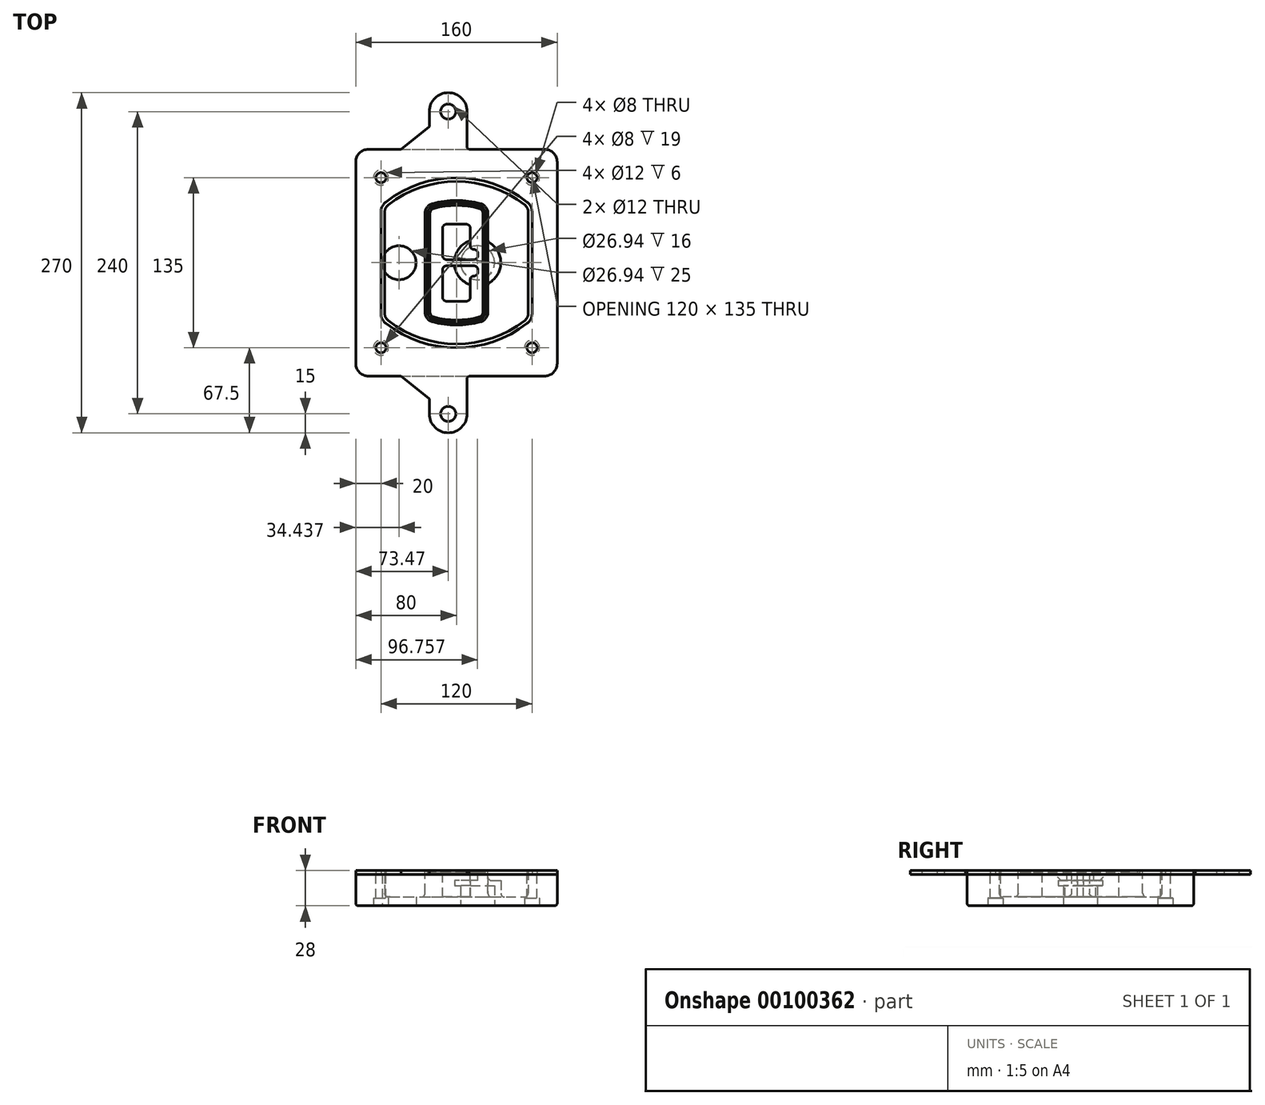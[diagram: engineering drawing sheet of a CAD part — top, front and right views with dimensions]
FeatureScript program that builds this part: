
annotation { "Feature Type Name" : "Feature", "Feature Type Description" : "" }
export const myFeature = defineFeature(function(context is Context, id is Id, definition is map)
    precondition{}
    {
        {
            var Q0;
            Q0=qCreatedBy(makeId("Top.planeOp"),FACE);
            var sketch = newSketch(context, id + "F0", { "sketchPlane" : qUnion([Q0])});
            skPoint(sketch, "E0.rect.middle", {"position": v(0, 0) * mm});
            skLineSegment(sketch, "E1.bottom", {"start": v(-70, -90) * mm, "end": v(70, -90) * mm});
            skLineSegment(sketch, "E1.top", {"start": v(-70, 90) * mm, "end": v(70, 90) * mm});
            skLineSegment(sketch, "E1.left", {"start": v(-80, -80) * mm, "end": v(-80, 80) * mm});
            skLineSegment(sketch, "E1.right", {"start": v(80, -80) * mm, "end": v(80, 80) * mm});
            skLineSegment(sketch, "E2", {"start": v(-80, 90) * mm, "end": v(80, -90) * mm, "construction": true});
            skLineSegment(sketch, "E3", {"start": v(80, 90) * mm, "end": v(-80, -90) * mm, "construction": true});
            skCircle(sketch, "E4", {"center": v(-60, 67.5) * mm, "radius": 4 * mm});
            skCircle(sketch, "E5", {"center": v(60, 67.5) * mm, "radius": 4 * mm});
            skCircle(sketch, "E6", {"center": v(60, -67.5) * mm, "radius": 4 * mm});
            skCircle(sketch, "E7", {"center": v(-60, -67.5) * mm, "radius": 4 * mm});
            skLineSegment(sketch, "E8", {"start": v(-60, 67.5) * mm, "end": v(60, 67.5) * mm, "construction": true});
            skLineSegment(sketch, "E9", {"start": v(60, 67.5) * mm, "end": v(60, -67.5) * mm, "construction": true});
            skLineSegment(sketch, "E10", {"start": v(60, -67.5) * mm, "end": v(-60, -67.5) * mm, "construction": true});
            skLineSegment(sketch, "E11", {"start": v(-60, -67.5) * mm, "end": v(-60, 67.5) * mm, "construction": true});
            skLineSegment(sketch, "E12", {"start": v(-60, 40.3) * mm, "end": v(-60, -40.3) * mm});
            skLineSegment(sketch, "E13", {"start": v(60, 40.3) * mm, "end": v(60, -40.3) * mm});
            skArc(sketch, "E14", {"start": v(56.15, 48.18) * mm, "mid": v(0, 67.5) * mm, "end": v(-56.15, 48.18) * mm});
            skArc(sketch, "E15", {"start": v(-56.15, -48.18) * mm, "mid": v(0, -67.5) * mm, "end": v(56.15, -48.18) * mm});
            skLineSegment(sketch, "E16", {"start": v(-60, 0) * mm, "end": v(60, 0) * mm, "construction": true});
            skPoint(sketch, "E17.visualSharp", {"position": v(-60, -45) * mm});
            skArc(sketch, "E17.filletArc", {"start": v(-60, -40.3) * mm, "mid": v(-58.99, -44.68) * mm, "end": v(-56.15, -48.18) * mm});
            skPoint(sketch, "E18.visualSharp", {"position": v(-60, 45) * mm});
            skArc(sketch, "E18.filletArc", {"start": v(-56.15, 48.18) * mm, "mid": v(-58.99, 44.68) * mm, "end": v(-60, 40.3) * mm});
            skPoint(sketch, "E19.visualSharp", {"position": v(60, 45) * mm});
            skArc(sketch, "E19.filletArc", {"start": v(60, 40.3) * mm, "mid": v(58.99, 44.68) * mm, "end": v(56.15, 48.18) * mm});
            skPoint(sketch, "E20.visualSharp", {"position": v(60, -45) * mm});
            skArc(sketch, "E20.filletArc", {"start": v(56.15, -48.18) * mm, "mid": v(58.99, -44.68) * mm, "end": v(60, -40.3) * mm});
            skPoint(sketch, "E21.visualSharp", {"position": v(-80, 90) * mm});
            skArc(sketch, "E21.filletArc", {"start": v(-70, 90) * mm, "mid": v(-77.07, 87.07) * mm, "end": v(-80, 80) * mm});
            skPoint(sketch, "E22.visualSharp", {"position": v(80, 90) * mm});
            skArc(sketch, "E22.filletArc", {"start": v(80, 80) * mm, "mid": v(77.07, 87.07) * mm, "end": v(70, 90) * mm});
            skPoint(sketch, "E23.visualSharp", {"position": v(80, -90) * mm});
            skArc(sketch, "E23.filletArc", {"start": v(70, -90) * mm, "mid": v(77.07, -87.07) * mm, "end": v(80, -80) * mm});
            skPoint(sketch, "E24.visualSharp", {"position": v(-80, -90) * mm});
            skArc(sketch, "E24.filletArc", {"start": v(-80, -80) * mm, "mid": v(-77.07, -87.07) * mm, "end": v(-70, -90) * mm});
            skArc(sketch, "E25.0", {"start": v(57, 40.3) * mm, "mid": v(56.3, 43.36) * mm, "end": v(54.3, 45.81) * mm});
            skLineSegment(sketch, "E25.1", {"start": v(57, 40.3) * mm, "end": v(57, -40.3) * mm});
            skArc(sketch, "E25.2", {"start": v(54.3, -45.81) * mm, "mid": v(56.3, -43.36) * mm, "end": v(57, -40.3) * mm});
            skArc(sketch, "E25.3", {"start": v(-54.3, -45.81) * mm, "mid": v(0, -64.5) * mm, "end": v(54.3, -45.81) * mm});
            skArc(sketch, "E25.4", {"start": v(-57, -40.3) * mm, "mid": v(-56.3, -43.36) * mm, "end": v(-54.3, -45.81) * mm});
            skArc(sketch, "E25.5", {"start": v(54.3, 45.81) * mm, "mid": v(0, 64.5) * mm, "end": v(-54.3, 45.81) * mm});
            skLineSegment(sketch, "E25.6", {"start": v(-57, 40.3) * mm, "end": v(-57, -40.3) * mm});
            skArc(sketch, "E25.7", {"start": v(-54.3, 45.81) * mm, "mid": v(-56.3, 43.36) * mm, "end": v(-57, 40.3) * mm});
            skArc(sketch, "E26.0", {"start": v(-58.62, 51.33) * mm, "mid": v(-62.58, 46.43) * mm, "end": v(-64, 40.3) * mm});
            skArc(sketch, "E26.1", {"start": v(58.62, 51.33) * mm, "mid": v(0, 71.5) * mm, "end": v(-58.62, 51.33) * mm});
            skArc(sketch, "E26.2", {"start": v(64, 40.3) * mm, "mid": v(62.58, 46.43) * mm, "end": v(58.62, 51.33) * mm});
            skLineSegment(sketch, "E26.3", {"start": v(64, 40.3) * mm, "end": v(64, -40.3) * mm});
            skArc(sketch, "E26.4", {"start": v(58.62, -51.33) * mm, "mid": v(62.58, -46.43) * mm, "end": v(64, -40.3) * mm});
            skLineSegment(sketch, "E26.5", {"start": v(-64, 40.3) * mm, "end": v(-64, -40.3) * mm});
            skArc(sketch, "E26.6", {"start": v(-58.62, -51.33) * mm, "mid": v(0, -71.5) * mm, "end": v(58.62, -51.33) * mm});
            skArc(sketch, "E26.7", {"start": v(-64, -40.3) * mm, "mid": v(-62.58, -46.43) * mm, "end": v(-58.62, -51.33) * mm});
            skSolve(sketch);
        }
        {
            var Q0;
            Q0=makeQuery(id+"F0.imprint","IMPRINT",FACE,{"disambiguationData":[TD([[makeQuery(id+"F0.imprint","IMPRINT",EDGE,{"derivedFrom":sQuery(id+"F0.wireOp",EDGE,"E1.bottom")}),1.0]])]});
            var Q1;
            Q1=makeQuery(id+"F0.imprint","IMPRINT",FACE,{"disambiguationData":[TD([[makeQuery(id+"F0.imprint","IMPRINT",EDGE,{"derivedFrom":sQuery(id+"F0.wireOp",EDGE,"E12")}),1.0]])]});
            var Q2;
            Q2=makeQuery(id+"F0.imprint","IMPRINT",FACE,{"disambiguationData":[TD([[makeQuery(id+"F0.imprint","IMPRINT",EDGE,{"derivedFrom":sQuery(id+"F0.wireOp",EDGE,"E25.0")}),1.0]])]});
            var Q3;
            Q3=makeQuery(id+"F0.imprint","IMPRINT",FACE,{"disambiguationData":[TD([[makeQuery(id+"F0.imprint","IMPRINT",EDGE,{"derivedFrom":sQuery(id+"F0.wireOp",EDGE,"E12")}),-1.0]])]});
            extrude(context, id + "F1", {"entities" : qUnion([Q0, Q1, Q2, Q3]), "oppositeDirection" : true, "depth" : 25 * mm});
        }
        {
            var Q0;
            Q0=makeQuery(id+"F0.imprint","IMPRINT",FACE,{"disambiguationData":[TD([[makeQuery(id+"F0.imprint","IMPRINT",EDGE,{"derivedFrom":sQuery(id+"F0.wireOp",EDGE,"E12")}),1.0]])]});
            extrude(context, id + "F2", {"entities" : qUnion([Q0]), "operationType" : NewBodyOperationType.ADD, "depth" : 3 * mm});
        }
        {
            var Q0;
            Q0=makeQuery(id+"F0.imprint","IMPRINT",FACE,{"disambiguationData":[TD([[makeQuery(id+"F0.imprint","IMPRINT",EDGE,{"derivedFrom":sQuery(id+"F0.wireOp",EDGE,"E25.0")}),1.0]])]});
            extrude(context, id + "F3", {"entities" : qUnion([Q0]), "operationType" : NewBodyOperationType.REMOVE, "oppositeDirection" : true, "depth" : 18 * mm});
        }
        {
            var Q0;
            Q0=makeQuery(id+"F2.opExtrude","CAP_FACE",FACE,{"disambiguationData":[OSD([sQuery(id+"F0.wireOp",EDGE,"E12"),sQuery(id+"F0.wireOp",EDGE,"E13"),sQuery(id+"F0.wireOp",EDGE,"E14"),sQuery(id+"F0.wireOp",EDGE,"E15"),sQuery(id+"F0.wireOp",EDGE,"E17.filletArc"),sQuery(id+"F0.wireOp",EDGE,"E18.filletArc"),sQuery(id+"F0.wireOp",EDGE,"E19.filletArc"),sQuery(id+"F0.wireOp",EDGE,"E20.filletArc"),sQuery(id+"F0.wireOp",EDGE,"E25.0"),sQuery(id+"F0.wireOp",EDGE,"E25.1"),sQuery(id+"F0.wireOp",EDGE,"E25.2"),sQuery(id+"F0.wireOp",EDGE,"E25.3"),sQuery(id+"F0.wireOp",EDGE,"E25.4"),sQuery(id+"F0.wireOp",EDGE,"E25.5"),sQuery(id+"F0.wireOp",EDGE,"E25.6"),sQuery(id+"F0.wireOp",EDGE,"E25.7")])],"isStart":false});
            var sketch = newSketch(context, id + "F4", { "sketchPlane" : qUnion([Q0])});
            skArc(sketch, "E27.0", {"start": v(-19.08, -46.97) * mm, "mid": v(0, -49.5) * mm, "end": v(19.08, -46.97) * mm});
            skArc(sketch, "E28.0", {"start": v(19.08, 46.97) * mm, "mid": v(0, 49.5) * mm, "end": v(-19.08, 46.97) * mm});
            skLineSegment(sketch, "E29", {"start": v(-25, 39.25) * mm, "end": v(-25, -39.25) * mm});
            skLineSegment(sketch, "E30", {"start": v(25, 39.25) * mm, "end": v(25, -39.25) * mm});
            skLineSegment(sketch, "E31", {"start": v(-25, 45.1) * mm, "end": v(25, 45.1) * mm, "construction": true});
            skLineSegment(sketch, "E32", {"start": v(-25, -45.1) * mm, "end": v(25, -45.1) * mm, "construction": true});
            skPoint(sketch, "E33.visualSharp", {"position": v(-25, 45.1) * mm});
            skArc(sketch, "E33.filletArc", {"start": v(-19.08, 46.97) * mm, "mid": v(-23.35, 44.11) * mm, "end": v(-25, 39.25) * mm});
            skPoint(sketch, "E34.visualSharp", {"position": v(25, 45.1) * mm});
            skArc(sketch, "E34.filletArc", {"start": v(25, 39.25) * mm, "mid": v(23.35, 44.11) * mm, "end": v(19.08, 46.97) * mm});
            skPoint(sketch, "E35.visualSharp", {"position": v(25, -45.1) * mm});
            skArc(sketch, "E35.filletArc", {"start": v(19.08, -46.97) * mm, "mid": v(23.35, -44.11) * mm, "end": v(25, -39.25) * mm});
            skPoint(sketch, "E36.visualSharp", {"position": v(-25, -45.1) * mm});
            skArc(sketch, "E36.filletArc", {"start": v(-25, -39.25) * mm, "mid": v(-23.35, -44.11) * mm, "end": v(-19.08, -46.97) * mm});
            skArc(sketch, "E37.0", {"start": v(54.3, 45.81) * mm, "mid": v(0, 64.5) * mm, "end": v(-54.3, 45.81) * mm});
            skArc(sketch, "E37.1", {"start": v(-54.3, 45.81) * mm, "mid": v(-56.3, 43.36) * mm, "end": v(-57, 40.3) * mm});
            skLineSegment(sketch, "E37.2", {"start": v(-57, 40.3) * mm, "end": v(-57, -40.3) * mm});
            skArc(sketch, "E37.3", {"start": v(-57, -40.3) * mm, "mid": v(-56.3, -43.36) * mm, "end": v(-54.3, -45.81) * mm});
            skArc(sketch, "E37.4", {"start": v(-54.3, -45.81) * mm, "mid": v(0, -64.5) * mm, "end": v(54.3, -45.81) * mm});
            skArc(sketch, "E37.5", {"start": v(54.3, -45.81) * mm, "mid": v(56.3, -43.36) * mm, "end": v(57, -40.3) * mm});
            skLineSegment(sketch, "E37.6", {"start": v(57, 40.3) * mm, "end": v(57, -40.3) * mm});
            skArc(sketch, "E37.7", {"start": v(57, 40.3) * mm, "mid": v(56.3, 43.36) * mm, "end": v(54.3, 45.81) * mm});
            skLineSegment(sketch, "E38.0", {"start": v(23, 39.25) * mm, "end": v(23, -39.25) * mm});
            skArc(sketch, "E38.1", {"start": v(18.56, -45.04) * mm, "mid": v(21.76, -42.9) * mm, "end": v(23, -39.25) * mm});
            skArc(sketch, "E38.2", {"start": v(-18.56, -45.04) * mm, "mid": v(0, -47.5) * mm, "end": v(18.56, -45.04) * mm});
            skArc(sketch, "E38.3", {"start": v(-23, -39.25) * mm, "mid": v(-21.76, -42.9) * mm, "end": v(-18.56, -45.04) * mm});
            skLineSegment(sketch, "E38.4", {"start": v(-23, 39.25) * mm, "end": v(-23, -39.25) * mm});
            skArc(sketch, "E38.5", {"start": v(23, 39.25) * mm, "mid": v(21.76, 42.9) * mm, "end": v(18.56, 45.04) * mm});
            skArc(sketch, "E38.6", {"start": v(-18.56, 45.04) * mm, "mid": v(-21.76, 42.9) * mm, "end": v(-23, 39.25) * mm});
            skArc(sketch, "E38.7", {"start": v(18.56, 45.04) * mm, "mid": v(0, 47.5) * mm, "end": v(-18.56, 45.04) * mm});
            skArc(sketch, "E39.0", {"start": v(21, 39.25) * mm, "mid": v(20.18, 41.68) * mm, "end": v(18.04, 43.1) * mm});
            skLineSegment(sketch, "E39.1", {"start": v(21, 39.25) * mm, "end": v(21, -39.25) * mm});
            skArc(sketch, "E39.2", {"start": v(18.04, -43.1) * mm, "mid": v(20.18, -41.68) * mm, "end": v(21, -39.25) * mm});
            skArc(sketch, "E39.3", {"start": v(-18.04, -43.1) * mm, "mid": v(0, -45.5) * mm, "end": v(18.04, -43.1) * mm});
            skArc(sketch, "E39.4", {"start": v(-21, -39.25) * mm, "mid": v(-20.18, -41.68) * mm, "end": v(-18.04, -43.1) * mm});
            skArc(sketch, "E39.5", {"start": v(18.04, 43.1) * mm, "mid": v(0, 45.5) * mm, "end": v(-18.04, 43.1) * mm});
            skLineSegment(sketch, "E39.6", {"start": v(-21, 39.25) * mm, "end": v(-21, -39.25) * mm});
            skArc(sketch, "E39.7", {"start": v(-18.04, 43.1) * mm, "mid": v(-20.18, 41.68) * mm, "end": v(-21, 39.25) * mm});
            skLineSegment(sketch, "E40", {"start": v(-25, 0) * mm, "end": v(25, 0) * mm, "construction": true});
            skLineSegment(sketch, "E41", {"start": v(-11, 5.5) * mm, "end": v(-11, 27.5) * mm});
            skLineSegment(sketch, "E42", {"start": v(-8, 30.5) * mm, "end": v(8, 30.5) * mm});
            skLineSegment(sketch, "E43", {"start": v(11, 27.5) * mm, "end": v(11, 13.5) * mm});
            skLineSegment(sketch, "E44", {"start": v(14, 10.5) * mm, "end": v(14, 10.5) * mm});
            skLineSegment(sketch, "E45", {"start": v(17, 7.5) * mm, "end": v(17, 5.5) * mm});
            skLineSegment(sketch, "E46", {"start": v(14, 2.5) * mm, "end": v(-8, 2.5) * mm});
            skPoint(sketch, "E47.visualSharp", {"position": v(-11, 30.5) * mm});
            skArc(sketch, "E47.filletArc", {"start": v(-8, 30.5) * mm, "mid": v(-10.12, 29.62) * mm, "end": v(-11, 27.5) * mm});
            skPoint(sketch, "E48.visualSharp", {"position": v(11, 30.5) * mm});
            skArc(sketch, "E48.filletArc", {"start": v(11, 27.5) * mm, "mid": v(10.12, 29.62) * mm, "end": v(8, 30.5) * mm});
            skPoint(sketch, "E49.visualSharp", {"position": v(11, 10.5) * mm});
            skArc(sketch, "E49.filletArc", {"start": v(11, 13.5) * mm, "mid": v(11.88, 11.38) * mm, "end": v(14, 10.5) * mm});
            skPoint(sketch, "E50.visualSharp", {"position": v(17, 10.5) * mm});
            skArc(sketch, "E50.filletArc", {"start": v(17, 7.5) * mm, "mid": v(16.12, 9.62) * mm, "end": v(14, 10.5) * mm});
            skPoint(sketch, "E51.visualSharp", {"position": v(17, 2.5) * mm});
            skArc(sketch, "E51.filletArc", {"start": v(14, 2.5) * mm, "mid": v(16.12, 3.38) * mm, "end": v(17, 5.5) * mm});
            skPoint(sketch, "E52.visualSharp", {"position": v(-11, 2.5) * mm});
            skArc(sketch, "E52.filletArc", {"start": v(-11, 5.5) * mm, "mid": v(-10.12, 3.38) * mm, "end": v(-8, 2.5) * mm});
            skLineSegment(sketch, "E53.0.MirrorCS", {"start": v(14, -2.5) * mm, "end": v(-8, -2.5) * mm});
            skArc(sketch, "E54.0.MirrorCS", {"start": v(-11, -5.5) * mm, "mid": v(-10.12, -3.38) * mm, "end": v(-8, -2.5) * mm});
            skLineSegment(sketch, "E55.0.MirrorCS", {"start": v(-11, -5.5) * mm, "end": v(-11, -27.5) * mm});
            skArc(sketch, "E56.0.MirrorCS", {"start": v(-8, -30.5) * mm, "mid": v(-10.12, -29.62) * mm, "end": v(-11, -27.5) * mm});
            skLineSegment(sketch, "E57.0.MirrorCS", {"start": v(-8, -30.5) * mm, "end": v(8, -30.5) * mm});
            skArc(sketch, "E58.0.MirrorCS", {"start": v(11, -27.5) * mm, "mid": v(10.12, -29.62) * mm, "end": v(8, -30.5) * mm});
            skLineSegment(sketch, "E59.0.MirrorCS", {"start": v(11, -27.5) * mm, "end": v(11, -13.5) * mm});
            skArc(sketch, "E60.0.MirrorCS", {"start": v(11, -13.5) * mm, "mid": v(11.88, -11.38) * mm, "end": v(14, -10.5) * mm});
            skArc(sketch, "E61.0.MirrorCS", {"start": v(17, -7.5) * mm, "mid": v(16.12, -9.62) * mm, "end": v(14, -10.5) * mm});
            skLineSegment(sketch, "E62.0.MirrorCS", {"start": v(17, -7.5) * mm, "end": v(17, -5.5) * mm});
            skArc(sketch, "E63.0.MirrorCS", {"start": v(14, -2.5) * mm, "mid": v(16.12, -3.38) * mm, "end": v(17, -5.5) * mm});
            skSolve(sketch);
        }
        {
            var Q0;
            Q0=makeQuery(id+"F4.imprint","IMPRINT",FACE,{"disambiguationData":[TD([[makeQuery(id+"F4.imprint","IMPRINT",EDGE,{"derivedFrom":sQuery(id+"F4.wireOp",EDGE,"E27.0")}),1.0]])]});
            var Q1;
            Q1=makeQuery(id+"F4.imprint","IMPRINT",FACE,{"disambiguationData":[TD([[makeQuery(id+"F4.imprint","IMPRINT",EDGE,{"derivedFrom":sQuery(id+"F4.wireOp",EDGE,"E38.0")}),-1.0]])]});
            var Q2;
            Q2=makeQuery(id+"F4.imprint","IMPRINT",FACE,{"disambiguationData":[TD([[makeQuery(id+"F4.imprint","IMPRINT",EDGE,{"derivedFrom":sQuery(id+"F4.wireOp",EDGE,"E39.0")}),1.0]])]});
            extrude(context, id + "F5", {"entities" : qUnion([Q0, Q1, Q2]), "operationType" : NewBodyOperationType.ADD, "endBound" : BoundingType.UP_TO_NEXT, "oppositeDirection" : true, "depth" : 25 * mm});
        }
        {
            var Q0;
            Q0=makeQuery(id+"F4.imprint","IMPRINT",FACE,{"disambiguationData":[TD([[makeQuery(id+"F4.imprint","IMPRINT",EDGE,{"derivedFrom":sQuery(id+"F4.wireOp",EDGE,"E38.0")}),-1.0]])]});
            extrude(context, id + "F6", {"entities" : qUnion([Q0]), "operationType" : NewBodyOperationType.REMOVE, "oppositeDirection" : true, "depth" : 2 * mm});
        }
        {
            var Q0;
            Q0=makeQuery(id+"F1.opExtrude","CAP_FACE",FACE,{"disambiguationData":[OSD([sQuery(id+"F0.wireOp",EDGE,"E1.bottom"),sQuery(id+"F0.wireOp",EDGE,"E1.top"),sQuery(id+"F0.wireOp",EDGE,"E1.left"),sQuery(id+"F0.wireOp",EDGE,"E1.right"),sQuery(id+"F0.wireOp",EDGE,"E4"),sQuery(id+"F0.wireOp",EDGE,"E5"),sQuery(id+"F0.wireOp",EDGE,"E6"),sQuery(id+"F0.wireOp",EDGE,"E7"),sQuery(id+"F0.wireOp",EDGE,"E21.filletArc"),sQuery(id+"F0.wireOp",EDGE,"E22.filletArc"),sQuery(id+"F0.wireOp",EDGE,"E23.filletArc"),sQuery(id+"F0.wireOp",EDGE,"E24.filletArc")])],"isStart":false});
            var sketch = newSketch(context, id + "F7", { "sketchPlane" : qUnion([Q0])});
            skCircle(sketch, "E64", {"center": v(16.76, 0) * mm, "radius": 13.47 * mm});
            skCircle(sketch, "E65", {"center": v(-45.56, 0) * mm, "radius": 13.47 * mm});
            skLineSegment(sketch, "E66", {"start": v(80, 0) * mm, "end": v(-80, 0) * mm});
            skCircle(sketch, "E67", {"center": v(16.76, 0) * mm, "radius": 18.47 * mm});
            skCircle(sketch, "E68", {"center": v(60, -67.5) * mm, "radius": 6 * mm});
            skCircle(sketch, "E69", {"center": v(-60, -67.5) * mm, "radius": 6 * mm});
            skCircle(sketch, "E70", {"center": v(-60, 67.5) * mm, "radius": 6 * mm});
            skCircle(sketch, "E71", {"center": v(60, 67.5) * mm, "radius": 6 * mm});
            skSolve(sketch);
        }
        {
            var Q0;
            {var subQ1=sQuery(id+"F7.wireOp",EDGE,"E66");var subQ4=sQuery(id+"F7.wireOp",EDGE,"E64");var subQ6=makeQuery(id+"F7.imprint","INTERSECT",VERTEX,{"disambiguationData":[OD(0.0)],"derivedFrom":[subQ4,subQ1]});Q0=makeQuery(id+"F7.imprint","IMPRINT",FACE,{"disambiguationData":[TD([[makeQuery(id+"F7.imprint","IMPRINT",EDGE,{"disambiguationData":[TD([[subQ6,-1.0]])],"derivedFrom":subQ4}),-1.0]])]});}
            var Q1;
            {var subQ0=sQuery(id+"F7.wireOp",EDGE,"E66");var subQ1=sQuery(id+"F7.wireOp",EDGE,"E64");var subQ3=makeQuery(id+"F7.imprint","INTERSECT",VERTEX,{"disambiguationData":[OD(0.0)],"derivedFrom":[subQ1,subQ0]});Q1=makeQuery(id+"F7.imprint","IMPRINT",FACE,{"disambiguationData":[TD([[makeQuery(id+"F7.imprint","IMPRINT",EDGE,{"disambiguationData":[TD([[subQ3,-1.0]])],"derivedFrom":subQ1}),1.0]])]});}
            var Q2;
            {var subQ0=sQuery(id+"F7.wireOp",EDGE,"E66");var subQ1=sQuery(id+"F7.wireOp",EDGE,"E64");var subQ3=makeQuery(id+"F7.imprint","INTERSECT",VERTEX,{"disambiguationData":[OD(0.0)],"derivedFrom":[subQ1,subQ0]});Q2=makeQuery(id+"F7.imprint","IMPRINT",FACE,{"disambiguationData":[TD([[makeQuery(id+"F7.imprint","IMPRINT",EDGE,{"disambiguationData":[TD([[subQ3,1.0]])],"derivedFrom":subQ1}),1.0]])]});}
            var Q3;
            {var subQ1=sQuery(id+"F7.wireOp",EDGE,"E66");var subQ4=sQuery(id+"F7.wireOp",EDGE,"E64");var subQ6=makeQuery(id+"F7.imprint","INTERSECT",VERTEX,{"disambiguationData":[OD(0.0)],"derivedFrom":[subQ4,subQ1]});Q3=makeQuery(id+"F7.imprint","IMPRINT",FACE,{"disambiguationData":[TD([[makeQuery(id+"F7.imprint","IMPRINT",EDGE,{"disambiguationData":[TD([[subQ6,1.0]])],"derivedFrom":subQ4}),-1.0]])]});}
            extrude(context, id + "F8", {"entities" : qUnion([Q0, Q1, Q2, Q3]), "operationType" : NewBodyOperationType.ADD, "oppositeDirection" : true, "depth" : 20 * mm});
        }
        {
            var Q0;
            {var subQ0=sQuery(id+"F7.wireOp",EDGE,"E66");var subQ1=sQuery(id+"F7.wireOp",EDGE,"E64");var subQ3=makeQuery(id+"F7.imprint","INTERSECT",VERTEX,{"disambiguationData":[OD(0.0)],"derivedFrom":[subQ1,subQ0]});Q0=makeQuery(id+"F7.imprint","IMPRINT",FACE,{"disambiguationData":[TD([[makeQuery(id+"F7.imprint","IMPRINT",EDGE,{"disambiguationData":[TD([[subQ3,-1.0]])],"derivedFrom":subQ1}),1.0]])]});}
            var Q1;
            {var subQ0=sQuery(id+"F7.wireOp",EDGE,"E66");var subQ1=sQuery(id+"F7.wireOp",EDGE,"E64");var subQ3=makeQuery(id+"F7.imprint","INTERSECT",VERTEX,{"disambiguationData":[OD(0.0)],"derivedFrom":[subQ1,subQ0]});Q1=makeQuery(id+"F7.imprint","IMPRINT",FACE,{"disambiguationData":[TD([[makeQuery(id+"F7.imprint","IMPRINT",EDGE,{"disambiguationData":[TD([[subQ3,1.0]])],"derivedFrom":subQ1}),1.0]])]});}
            extrude(context, id + "F9", {"entities" : qUnion([Q0, Q1]), "operationType" : NewBodyOperationType.REMOVE, "oppositeDirection" : true, "depth" : 16 * mm});
        }
        {
            var Q0;
            {var subQ0=sQuery(id+"F7.wireOp",EDGE,"E66");var subQ1=sQuery(id+"F7.wireOp",EDGE,"E65");var subQ3=makeQuery(id+"F7.imprint","INTERSECT",VERTEX,{"disambiguationData":[OD(0.0)],"derivedFrom":[subQ1,subQ0]});Q0=makeQuery(id+"F7.imprint","IMPRINT",FACE,{"disambiguationData":[TD([[makeQuery(id+"F7.imprint","IMPRINT",EDGE,{"disambiguationData":[TD([[subQ3,-1.0]])],"derivedFrom":subQ1}),1.0]])]});}
            var Q1;
            {var subQ0=sQuery(id+"F7.wireOp",EDGE,"E66");var subQ1=sQuery(id+"F7.wireOp",EDGE,"E65");var subQ3=makeQuery(id+"F7.imprint","INTERSECT",VERTEX,{"disambiguationData":[OD(0.0)],"derivedFrom":[subQ1,subQ0]});Q1=makeQuery(id+"F7.imprint","IMPRINT",FACE,{"disambiguationData":[TD([[makeQuery(id+"F7.imprint","IMPRINT",EDGE,{"disambiguationData":[TD([[subQ3,1.0]])],"derivedFrom":subQ1}),1.0]])]});}
            extrude(context, id + "F10", {"entities" : qUnion([Q0, Q1]), "operationType" : NewBodyOperationType.REMOVE, "oppositeDirection" : true, "depth" : 25 * mm});
        }
        {
            var Q0;
            Q0=makeQuery(id+"F7.imprint","IMPRINT",FACE,{"disambiguationData":[TD([[makeQuery(id+"F7.imprint","IMPRINT",EDGE,{"derivedFrom":sQuery(id+"F7.wireOp",EDGE,"E68")}),1.0]])]});
            var Q1;
            Q1=makeQuery(id+"F7.imprint","IMPRINT",FACE,{"disambiguationData":[TD([[makeQuery(id+"F7.imprint","IMPRINT",EDGE,{"derivedFrom":makeQuery(id+"F1.opExtrude","CAP_EDGE",EDGE,{"disambiguationData":[OSD([sQuery(id+"F0.wireOp",EDGE,"E5")])],"isStart":false})}),-1.0]])]});
            var Q2;
            Q2=makeQuery(id+"F7.imprint","IMPRINT",FACE,{"disambiguationData":[TD([[makeQuery(id+"F7.imprint","IMPRINT",EDGE,{"derivedFrom":sQuery(id+"F7.wireOp",EDGE,"E69")}),1.0]])]});
            var Q3;
            Q3=makeQuery(id+"F7.imprint","IMPRINT",FACE,{"disambiguationData":[TD([[makeQuery(id+"F7.imprint","IMPRINT",EDGE,{"derivedFrom":makeQuery(id+"F1.opExtrude","CAP_EDGE",EDGE,{"disambiguationData":[OSD([sQuery(id+"F0.wireOp",EDGE,"E4")])],"isStart":false})}),-1.0]])]});
            var Q4;
            Q4=makeQuery(id+"F7.imprint","IMPRINT",FACE,{"disambiguationData":[TD([[makeQuery(id+"F7.imprint","IMPRINT",EDGE,{"derivedFrom":sQuery(id+"F7.wireOp",EDGE,"E70")}),1.0]])]});
            var Q5;
            Q5=makeQuery(id+"F7.imprint","IMPRINT",FACE,{"disambiguationData":[TD([[makeQuery(id+"F7.imprint","IMPRINT",EDGE,{"derivedFrom":makeQuery(id+"F1.opExtrude","CAP_EDGE",EDGE,{"disambiguationData":[OSD([sQuery(id+"F0.wireOp",EDGE,"E7")])],"isStart":false})}),-1.0]])]});
            var Q6;
            Q6=makeQuery(id+"F7.imprint","IMPRINT",FACE,{"disambiguationData":[TD([[makeQuery(id+"F7.imprint","IMPRINT",EDGE,{"derivedFrom":sQuery(id+"F7.wireOp",EDGE,"E71")}),1.0]])]});
            var Q7;
            Q7=makeQuery(id+"F7.imprint","IMPRINT",FACE,{"disambiguationData":[TD([[makeQuery(id+"F7.imprint","IMPRINT",EDGE,{"derivedFrom":makeQuery(id+"F1.opExtrude","CAP_EDGE",EDGE,{"disambiguationData":[OSD([sQuery(id+"F0.wireOp",EDGE,"E6")])],"isStart":false})}),-1.0]])]});
            extrude(context, id + "F11", {"entities" : qUnion([Q0, Q1, Q2, Q3, Q4, Q5, Q6, Q7]), "operationType" : NewBodyOperationType.REMOVE, "oppositeDirection" : true, "depth" : 6 * mm});
        }
        {
            var Q0;
            Q0=makeQuery(id+"F9.boolean.opBoolean","COPY",FACE,{"derivedFrom":makeQuery(id+"F9.opExtrude","CAP_FACE",FACE,{"disambiguationData":[OSD([sQuery(id+"F7.wireOp",EDGE,"E64")])],"isStart":false})});
            var sketch = newSketch(context, id + "F12", { "sketchPlane" : qUnion([Q0])});
            skArc(sketch, "E72.0", {"start": v(11, 17.55) * mm, "mid": v(2.57, 11.82) * mm, "end": v(-1.54, 2.5) * mm});
            skArc(sketch, "E72.1", {"start": v(-1.54, -2.5) * mm, "mid": v(2.57, -11.82) * mm, "end": v(11, -17.55) * mm});
            skLineSegment(sketch, "E73", {"start": v(-1.54, -2.5) * mm, "end": v(14, -2.5) * mm});
            skLineSegment(sketch, "E74.0", {"start": v(14, 2.5) * mm, "end": v(-1.54, 2.5) * mm});
            skArc(sketch, "E74.1", {"start": v(14, 2.5) * mm, "mid": v(16.12, 3.38) * mm, "end": v(17, 5.5) * mm});
            skLineSegment(sketch, "E74.2", {"start": v(17, 7.5) * mm, "end": v(17, 5.5) * mm});
            skArc(sketch, "E74.3", {"start": v(17, 7.5) * mm, "mid": v(16.12, 9.62) * mm, "end": v(14, 10.5) * mm});
            skArc(sketch, "E74.4", {"start": v(11, 13.5) * mm, "mid": v(11.88, 11.38) * mm, "end": v(14, 10.5) * mm});
            skLineSegment(sketch, "E74.5", {"start": v(11, 17.55) * mm, "end": v(11, 13.5) * mm});
            skLineSegment(sketch, "E74.7", {"start": v(14, -2.5) * mm, "end": v(-1.54, -2.5) * mm});
            skArc(sketch, "E74.8", {"start": v(14, -2.5) * mm, "mid": v(16.12, -3.38) * mm, "end": v(17, -5.5) * mm});
            skLineSegment(sketch, "E74.9", {"start": v(17, -7.5) * mm, "end": v(17, -5.5) * mm});
            skArc(sketch, "E74.10", {"start": v(17, -7.5) * mm, "mid": v(16.12, -9.62) * mm, "end": v(14, -10.5) * mm});
            skArc(sketch, "E74.11", {"start": v(11, -13.5) * mm, "mid": v(11.88, -11.38) * mm, "end": v(14, -10.5) * mm});
            skLineSegment(sketch, "E74.12", {"start": v(11, -17.55) * mm, "end": v(11, -13.5) * mm});
            skPoint(sketch, "E75.orphan", {"position": v(11, -27.5) * mm});
            skPoint(sketch, "E76.orphan", {"position": v(-8, -2.5) * mm});
            skPoint(sketch, "E77.orphan", {"position": v(-8, 2.5) * mm});
            skPoint(sketch, "E78.orphan", {"position": v(11, 27.5) * mm});
            skSolve(sketch);
        }
        {
            var Q0;
            {var subQ7=sQuery(id+"F12.wireOp",EDGE,"E72.0");var subQ14=sQuery(id+"F12.wireOp",EDGE,"E72.1");var subQ16=sQuery(id+"F12.wireOp",EDGE,"E74.1");var subQ18=sQuery(id+"F12.wireOp",EDGE,"E74.8");Q0=qUnion([makeQuery(id+"F12.imprint","IMPRINT",FACE,{"disambiguationData":[TD([[makeQuery(id+"F12.imprint","IMPRINT",EDGE,{"derivedFrom":subQ7}),1.0]])]}),makeQuery(id+"F12.imprint","IMPRINT",FACE,{"disambiguationData":[TD([[makeQuery(id+"F12.imprint","IMPRINT",EDGE,{"derivedFrom":subQ14}),1.0]])]}),makeQuery(id+"F12.imprint","IMPRINT",FACE,{"disambiguationData":[TD([[makeQuery(id+"F12.imprint","IMPRINT",EDGE,{"derivedFrom":subQ16}),1.0]])]}),makeQuery(id+"F12.imprint","IMPRINT",FACE,{"disambiguationData":[TD([[makeQuery(id+"F12.imprint","IMPRINT",EDGE,{"derivedFrom":subQ18}),-1.0]])]})]);}
            var Q1;
            Q1=makeQuery(id+"F5.boolean.opBoolean","SPLIT",FACE,{"disambiguationData":[TD([makeQuery(id+"F5.opExtrude","SWEPT_FACE",FACE,{"disambiguationData":[OSD([sQuery(id+"F4.wireOp",EDGE,"E41")])]})])],"derivedFrom":makeQuery(id+"F3.boolean.opBoolean","COPY",FACE,{"derivedFrom":makeQuery(id+"F3.opExtrude","CAP_FACE",FACE,{"disambiguationData":[OSD([sQuery(id+"F0.wireOp",EDGE,"E25.0"),sQuery(id+"F0.wireOp",EDGE,"E25.1"),sQuery(id+"F0.wireOp",EDGE,"E25.2"),sQuery(id+"F0.wireOp",EDGE,"E25.3"),sQuery(id+"F0.wireOp",EDGE,"E25.4"),sQuery(id+"F0.wireOp",EDGE,"E25.5"),sQuery(id+"F0.wireOp",EDGE,"E25.6"),sQuery(id+"F0.wireOp",EDGE,"E25.7")])],"isStart":false})})});
            extrude(context, id + "F13", {"entities" : qUnion([Q0]), "operationType" : NewBodyOperationType.REMOVE, "endBound" : BoundingType.UP_TO_SURFACE, "endBoundEntityFace" : qUnion([Q1]), "depth" : 25 * mm});
        }
        {
            var Q0;
            Q0=makeQuery(id+"F3.boolean.opBoolean","COPY",EDGE,{"derivedFrom":makeQuery(id+"F3.opExtrude","CAP_EDGE",EDGE,{"disambiguationData":[OSD([sQuery(id+"F0.wireOp",EDGE,"E25.6")])],"isStart":false})});
            var Q1;
            Q1=makeQuery(id+"F8.boolean.opBoolean","INTERSECT",EDGE,{"derivedFrom":[makeQuery(id+"F5.opExtrude","SWEPT_FACE",FACE,{"disambiguationData":[OSD([sQuery(id+"F4.wireOp",EDGE,"E30")])]}),makeQuery(id+"F8.opExtrude","CAP_FACE",FACE,{"disambiguationData":[OSD([sQuery(id+"F7.wireOp",EDGE,"E67")])],"isStart":false})]});
            var Q2;
            Q2=makeQuery(id+"F8.boolean.opBoolean","INTERSECT",EDGE,{"disambiguationData":[OD(1.0)],"derivedFrom":[makeQuery(id+"F5.opExtrude","SWEPT_FACE",FACE,{"disambiguationData":[OSD([sQuery(id+"F4.wireOp",EDGE,"E30")])]}),makeQuery(id+"F8.opExtrude","SWEPT_FACE",FACE,{"disambiguationData":[OSD([sQuery(id+"F7.wireOp",EDGE,"E67")])]})]});
            var Q3;
            {var subQ0=sQuery(id+"F4.wireOp",EDGE,"E30");Q3=makeQuery(id+"F8.boolean.opBoolean","SPLIT",EDGE,{"disambiguationData":[TD([makeQuery(id+"F5.opExtrude","SWEPT_FACE",FACE,{"disambiguationData":[OSD([sQuery(id+"F4.wireOp",EDGE,"E35.filletArc")])]})])],"derivedFrom":makeQuery(id+"F5.opExtrude","CAP_EDGE",EDGE,{"disambiguationData":[OSD([subQ0])],"isStart":false})});}
            var Q4;
            {var subQ0=sQuery(id+"F0.wireOp",EDGE,"E25.7");var subQ1=sQuery(id+"F0.wireOp",EDGE,"E25.1");var subQ2=sQuery(id+"F0.wireOp",EDGE,"E25.6");var subQ3=sQuery(id+"F0.wireOp",EDGE,"E25.5");var subQ4=sQuery(id+"F0.wireOp",EDGE,"E25.4");var subQ5=sQuery(id+"F0.wireOp",EDGE,"E25.0");var subQ6=sQuery(id+"F0.wireOp",EDGE,"E25.2");var subQ7=sQuery(id+"F0.wireOp",EDGE,"E25.3");Q4=makeQuery(id+"F8.boolean.opBoolean","INTERSECT",EDGE,{"derivedFrom":[makeQuery(id+"F5.boolean.opBoolean","SPLIT",FACE,{"disambiguationData":[TD([makeQuery(id+"F2.opExtrude","SWEPT_FACE",FACE,{"disambiguationData":[OSD([subQ5])]})])],"derivedFrom":makeQuery(id+"F3.boolean.opBoolean","COPY",FACE,{"derivedFrom":makeQuery(id+"F3.opExtrude","CAP_FACE",FACE,{"disambiguationData":[OSD([subQ5,subQ1,subQ6,subQ7,subQ4,subQ3,subQ2,subQ0])],"isStart":false})})}),makeQuery(id+"F8.opExtrude","SWEPT_FACE",FACE,{"disambiguationData":[OSD([sQuery(id+"F7.wireOp",EDGE,"E67")])]})]});}
            var Q5;
            Q5=makeQuery(id+"F8.boolean.opBoolean","INTERSECT",EDGE,{"disambiguationData":[OD(0.0)],"derivedFrom":[makeQuery(id+"F5.opExtrude","SWEPT_FACE",FACE,{"disambiguationData":[OSD([sQuery(id+"F4.wireOp",EDGE,"E30")])]}),makeQuery(id+"F8.opExtrude","SWEPT_FACE",FACE,{"disambiguationData":[OSD([sQuery(id+"F7.wireOp",EDGE,"E67")])]})]});
            fillet(context, id + "F14", {"entities" : qUnion([Q0, Q1, Q2, Q3, Q4, Q5]), "radius" : 3 * mm, "tangentPropagation" : true, "allowEdgeOverflow" : false});
        }
        {
            var Q0;
            Q0=makeQuery(id+"F1.opExtrude","CAP_EDGE",EDGE,{"disambiguationData":[OSD([sQuery(id+"F0.wireOp",EDGE,"E1.bottom")])],"isStart":false});
            fillet(context, id + "F15", {"entities" : qUnion([Q0]), "radius" : 2 * mm, "tangentPropagation" : true, "allowEdgeOverflow" : false});
        }
        {
            var Q0;
            {var subQ0=sQuery(id+"F0.wireOp",EDGE,"E22.filletArc");var subQ1=sQuery(id+"F0.wireOp",EDGE,"E7");var subQ2=sQuery(id+"F0.wireOp",EDGE,"E6");var subQ3=sQuery(id+"F0.wireOp",EDGE,"E5");var subQ4=sQuery(id+"F0.wireOp",EDGE,"E4");var subQ5=sQuery(id+"F0.wireOp",EDGE,"E1.bottom");var subQ6=sQuery(id+"F0.wireOp",EDGE,"E21.filletArc");var subQ7=sQuery(id+"F0.wireOp",EDGE,"E1.top");var subQ8=sQuery(id+"F0.wireOp",EDGE,"E1.left");var subQ9=sQuery(id+"F0.wireOp",EDGE,"E1.right");var subQ10=sQuery(id+"F0.wireOp",EDGE,"E23.filletArc");var subQ11=sQuery(id+"F0.wireOp",EDGE,"E24.filletArc");Q0=makeQuery(id+"F2.boolean.opBoolean","SPLIT",FACE,{"disambiguationData":[TD([makeQuery(id+"F1.opExtrude","SWEPT_FACE",FACE,{"disambiguationData":[OSD([subQ5])]})])],"derivedFrom":makeQuery(id+"F1.opExtrude","CAP_FACE",FACE,{"disambiguationData":[OSD([subQ5,subQ7,subQ8,subQ9,subQ4,subQ3,subQ2,subQ1,subQ6,subQ0,subQ10,subQ11])],"isStart":true})});}
            var sketch = newSketch(context, id + "F16", { "sketchPlane" : qUnion([Q0])});
            skLineSegment(sketch, "E79", {"start": v(-21.53, 108) * mm, "end": v(-21.53, 120) * mm});
            skLineSegment(sketch, "E80", {"start": v(9.83, 90) * mm, "end": v(8.47, 91.36) * mm});
            skLineSegment(sketch, "E81", {"start": v(8.47, 91.36) * mm, "end": v(8.47, 120) * mm});
            skLineSegment(sketch, "E82", {"start": v(-6.53, 120) * mm, "end": v(-6.53, 90) * mm, "construction": true});
            skCircle(sketch, "E83", {"center": v(-6.53, 120) * mm, "radius": 6 * mm});
            skArc(sketch, "E84", {"start": v(8.47, 120) * mm, "mid": v(-6.53, 135) * mm, "end": v(-21.53, 120) * mm});
            skLineSegment(sketch, "E85.trimOffspring", {"start": v(-21.53, 108) * mm, "end": v(-44.03, 90) * mm});
            skLineSegment(sketch, "E86", {"start": v(-80, 0) * mm, "end": v(80, 0) * mm, "construction": true});
            skLineSegment(sketch, "E87.MirrorCS", {"start": v(-21.53, -108) * mm, "end": v(-21.53, -120) * mm});
            skLineSegment(sketch, "E88.MirrorCS", {"start": v(-6.53, -120) * mm, "end": v(-6.53, -90) * mm, "construction": true});
            skCircle(sketch, "E89.MirrorC", {"center": v(-6.53, -120) * mm, "radius": 6 * mm});
            skLineSegment(sketch, "E90.MirrorCS", {"start": v(-21.53, -108) * mm, "end": v(-44.03, -90) * mm});
            skLineSegment(sketch, "E91.MirrorCS", {"start": v(8.47, -91.36) * mm, "end": v(8.47, -120) * mm});
            skLineSegment(sketch, "E92.MirrorCS", {"start": v(9.83, -90) * mm, "end": v(8.47, -91.36) * mm});
            skArc(sketch, "E93.MirrorCS", {"start": v(8.47, -120) * mm, "mid": v(-6.53, -135) * mm, "end": v(-21.53, -120) * mm});
            skSolve(sketch);
        }
        {
            var Q0;
            Q0=makeQuery(id+"F16.imprint","IMPRINT",FACE,{"disambiguationData":[TD([[makeQuery(id+"F16.imprint","IMPRINT",EDGE,{"derivedFrom":sQuery(id+"F16.wireOp",EDGE,"E79")}),-1.0]])]});
            var Q1;
            Q1=makeQuery(id+"F16.imprint","IMPRINT",FACE,{"disambiguationData":[TD([[makeQuery(id+"F16.imprint","IMPRINT",EDGE,{"derivedFrom":makeQuery(id+"F1.opExtrude","CAP_EDGE",EDGE,{"disambiguationData":[OSD([sQuery(id+"F0.wireOp",EDGE,"E1.left")])],"isStart":true})}),-1.0]])]});
            var Q2;
            Q2=makeQuery(id+"F16.imprint","IMPRINT",FACE,{"disambiguationData":[TD([[makeQuery(id+"F16.imprint","IMPRINT",EDGE,{"derivedFrom":sQuery(id+"F16.wireOp",EDGE,"E87.MirrorCS")}),1.0]])]});
            var Q3;
            Q3=makeQuery(id+"F2.opExtrude","CAP_FACE",FACE,{"disambiguationData":[OSD([sQuery(id+"F0.wireOp",EDGE,"E12"),sQuery(id+"F0.wireOp",EDGE,"E13"),sQuery(id+"F0.wireOp",EDGE,"E14"),sQuery(id+"F0.wireOp",EDGE,"E15"),sQuery(id+"F0.wireOp",EDGE,"E17.filletArc"),sQuery(id+"F0.wireOp",EDGE,"E18.filletArc"),sQuery(id+"F0.wireOp",EDGE,"E19.filletArc"),sQuery(id+"F0.wireOp",EDGE,"E20.filletArc"),sQuery(id+"F0.wireOp",EDGE,"E25.0"),sQuery(id+"F0.wireOp",EDGE,"E25.1"),sQuery(id+"F0.wireOp",EDGE,"E25.2"),sQuery(id+"F0.wireOp",EDGE,"E25.3"),sQuery(id+"F0.wireOp",EDGE,"E25.4"),sQuery(id+"F0.wireOp",EDGE,"E25.5"),sQuery(id+"F0.wireOp",EDGE,"E25.6"),sQuery(id+"F0.wireOp",EDGE,"E25.7")])],"isStart":false});
            extrude(context, id + "F17", {"entities" : qUnion([Q0, Q1, Q2]), "endBound" : BoundingType.UP_TO_SURFACE, "endBoundEntityFace" : qUnion([Q3]), "depth" : 25 * mm});
        }
    });
